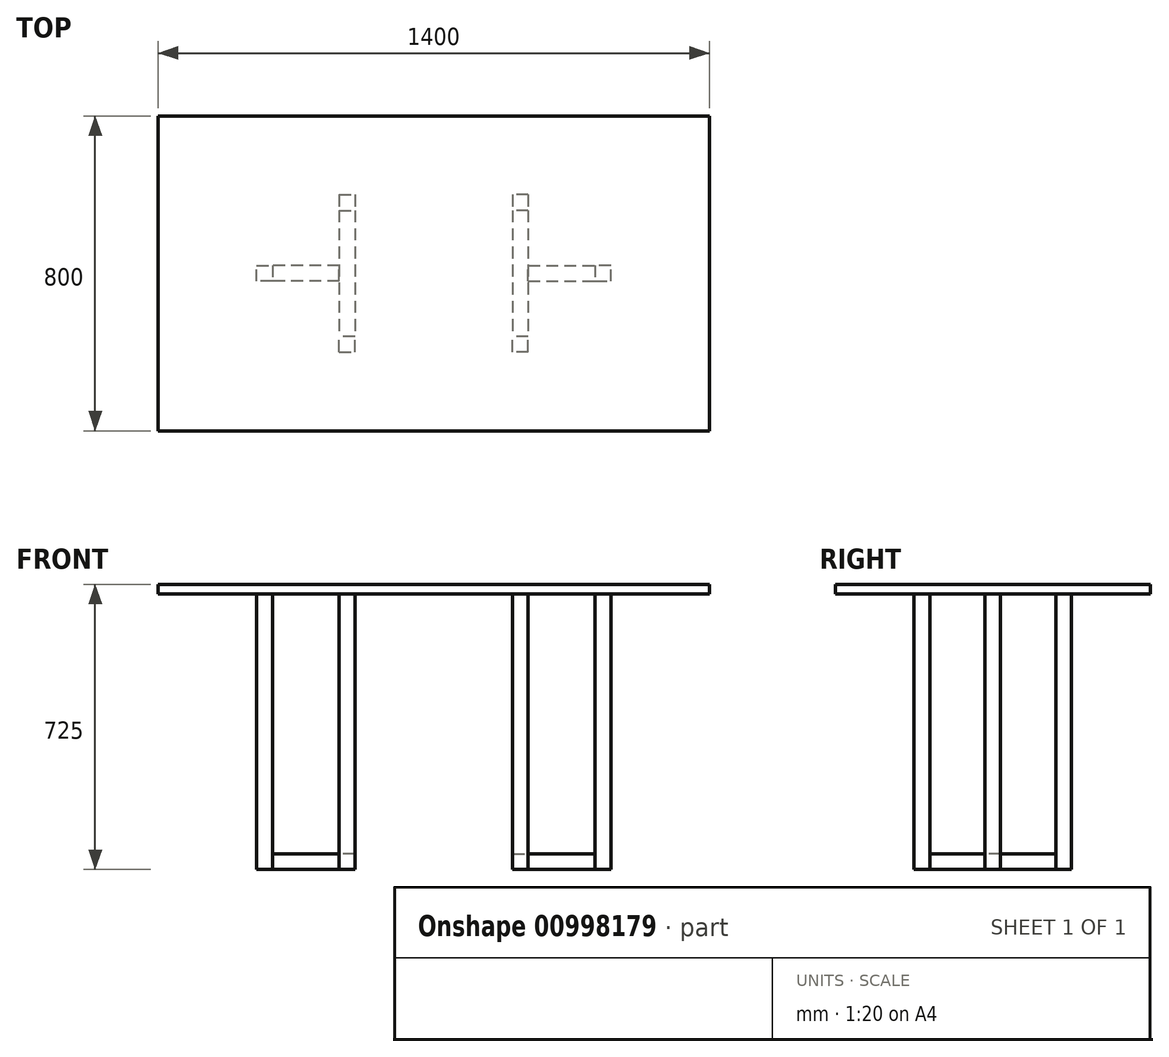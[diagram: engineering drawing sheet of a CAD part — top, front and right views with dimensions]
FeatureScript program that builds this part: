
annotation { "Feature Type Name" : "Feature", "Feature Type Description" : "" }
export const myFeature = defineFeature(function(context is Context, id is Id, definition is map)
    precondition{}
    {
        {
            var Q0;
            Q0=qCreatedBy(makeId("Top.planeOp"),FACE);
            var sketch = newSketch(context, id + "F0", { "sketchPlane" : qUnion([Q0])});
            skLineSegment(sketch, "E0.bottom", {"start": v(0, 0) * mm, "end": v(-1400, 0) * mm, "construction": true});
            skLineSegment(sketch, "E0.top", {"start": v(0, 800) * mm, "end": v(-1400, 800) * mm, "construction": true});
            skLineSegment(sketch, "E0.left", {"start": v(0, 0) * mm, "end": v(0, 800) * mm, "construction": true});
            skLineSegment(sketch, "E0.right", {"start": v(-1400, 0) * mm, "end": v(-1400, 800) * mm, "construction": true});
            skLineSegment(sketch, "E1", {"start": v(-1400, 800) * mm, "end": v(-1400, 600) * mm, "construction": true});
            skLineSegment(sketch, "E2", {"start": v(-700, 800) * mm, "end": v(-700, 0) * mm, "construction": true});
            skLineSegment(sketch, "E3", {"start": v(-1400, 400) * mm, "end": v(0, 400) * mm, "construction": true});
            skLineSegment(sketch, "E4", {"start": v(-1400, 400) * mm, "end": v(-1150, 400) * mm, "construction": true});
            skLineSegment(sketch, "E5", {"start": v(-1400, 600) * mm, "end": v(-940, 600) * mm, "construction": true});
            skLineSegment(sketch, "E6.bottom", {"start": v(-940, 600) * mm, "end": v(-900, 600) * mm});
            skLineSegment(sketch, "E6.top", {"start": v(-940, 560) * mm, "end": v(-900, 560) * mm});
            skLineSegment(sketch, "E6.left", {"start": v(-940, 600) * mm, "end": v(-940, 560) * mm});
            skLineSegment(sketch, "E6.right", {"start": v(-900, 600) * mm, "end": v(-900, 560) * mm});
            skLineSegment(sketch, "E7", {"start": v(-1150, 400) * mm, "end": v(-1150, 420) * mm});
            skLineSegment(sketch, "E8", {"start": v(-1150, 420) * mm, "end": v(-1110, 420) * mm});
            skLineSegment(sketch, "E9", {"start": v(-1110, 420) * mm, "end": v(-1110, 380) * mm});
            skLineSegment(sketch, "E10", {"start": v(-1110, 380) * mm, "end": v(-1150, 380) * mm});
            skLineSegment(sketch, "E11", {"start": v(-1150, 380) * mm, "end": v(-1150, 400) * mm});
            skLineSegment(sketch, "E12.MirrorCS", {"start": v(-940, 240) * mm, "end": v(-900, 240) * mm});
            skLineSegment(sketch, "E13.MirrorCS", {"start": v(-900, 200) * mm, "end": v(-900, 240) * mm});
            skLineSegment(sketch, "E14.MirrorCS", {"start": v(-940, 200) * mm, "end": v(-900, 200) * mm});
            skLineSegment(sketch, "E15.MirrorCS", {"start": v(-940, 200) * mm, "end": v(-940, 240) * mm});
            skLineSegment(sketch, "E16.MirrorCS", {"start": v(-250, 420) * mm, "end": v(-290, 420) * mm});
            skLineSegment(sketch, "E17.MirrorCS", {"start": v(-290, 420) * mm, "end": v(-290, 380) * mm});
            skLineSegment(sketch, "E18.MirrorCS", {"start": v(-290, 380) * mm, "end": v(-250, 380) * mm});
            skLineSegment(sketch, "E19.MirrorCS", {"start": v(-250, 380) * mm, "end": v(-250, 400) * mm});
            skLineSegment(sketch, "E20.MirrorCS", {"start": v(-500, 600) * mm, "end": v(-500, 560) * mm});
            skLineSegment(sketch, "E21.MirrorCS", {"start": v(-460, 600) * mm, "end": v(-500, 600) * mm});
            skLineSegment(sketch, "E22.MirrorCS", {"start": v(-460, 600) * mm, "end": v(-460, 560) * mm});
            skLineSegment(sketch, "E23.MirrorCS", {"start": v(-460, 560) * mm, "end": v(-500, 560) * mm});
            skLineSegment(sketch, "E24.MirrorCS", {"start": v(-500, 200) * mm, "end": v(-500, 240) * mm});
            skLineSegment(sketch, "E25.MirrorCS", {"start": v(-460, 240) * mm, "end": v(-500, 240) * mm});
            skLineSegment(sketch, "E26.MirrorCS", {"start": v(-460, 200) * mm, "end": v(-460, 240) * mm});
            skLineSegment(sketch, "E27.MirrorCS", {"start": v(-460, 200) * mm, "end": v(-500, 200) * mm});
            skLineSegment(sketch, "E28.MirrorCS", {"start": v(-250, 400) * mm, "end": v(-250, 420) * mm});
            skSolve(sketch);
        }
        {
            var Q0;
            Q0 = qSketchRegion(id + "F0", true);
            extrude(context, id + "F1", {"entities" : qUnion([Q0]), "depth" : 700 * mm, "offsetDistance" : 25 * mm});
        }
        {
            var Q0;
            Q0=makeQuery(id+"F1.opExtrude","SWEPT_FACE",FACE,{"disambiguationData":[OSD([sQuery(id+"F0.wireOp",EDGE,"E12.MirrorCS")])]});
            cPlane(context, id + "F2", {"entities" : qUnion([Q0]), "cplaneType" : CPlaneType.OFFSET, "offset" : 0 * mm, "width" : 150 * mm, "height" : 150 * mm});
        }
        {
            var Q0;
            Q0=qCreatedBy(id+"F2.planeOp",FACE);
            var sketch = newSketch(context, id + "F3", { "sketchPlane" : qUnion([Q0])});
            skLineSegment(sketch, "E29", {"start": v(460, 0) * mm, "end": v(500, 0) * mm});
            skLineSegment(sketch, "E30", {"start": v(500, 0) * mm, "end": v(500, 40) * mm});
            skLineSegment(sketch, "E31", {"start": v(500, 40) * mm, "end": v(460, 40) * mm});
            skLineSegment(sketch, "E32", {"start": v(460, 40) * mm, "end": v(460, 0) * mm});
            skLineSegment(sketch, "E33", {"start": v(700, 0) * mm, "end": v(700, 149.7) * mm, "construction": true});
            skLineSegment(sketch, "E34.MirrorCS", {"start": v(900, 40) * mm, "end": v(940, 40) * mm});
            skLineSegment(sketch, "E35.MirrorCS", {"start": v(940, 40) * mm, "end": v(940, 0) * mm});
            skLineSegment(sketch, "E36.MirrorCS", {"start": v(900, 0) * mm, "end": v(900, 40) * mm});
            skLineSegment(sketch, "E37.MirrorCS", {"start": v(940, 0) * mm, "end": v(900, 0) * mm});
            skSolve(sketch);
        }
        {
            var Q0;
            Q0 = qSketchRegion(id + "F3", true);
            extrude(context, id + "F4", {"entities" : qUnion([Q0]), "depth" : 320 * mm, "offsetDistance" : 25 * mm});
        }
        {
            var Q0;
            Q0=makeQuery(id+"F1.opExtrude","SWEPT_FACE",FACE,{"disambiguationData":[OSD([sQuery(id+"F0.wireOp",EDGE,"E17.MirrorCS")])]});
            cPlane(context, id + "F5", {"entities" : qUnion([Q0]), "cplaneType" : CPlaneType.OFFSET, "offset" : 0 * mm, "width" : 150 * mm, "height" : 150 * mm});
        }
        {
            var Q0;
            Q0=qCreatedBy(id+"F5.planeOp",FACE);
            var sketch = newSketch(context, id + "F6", { "sketchPlane" : qUnion([Q0])});
            skLineSegment(sketch, "E38", {"start": v(0, 0) * mm, "end": v(-400, 0) * mm, "construction": true});
            skLineSegment(sketch, "E39", {"start": v(-400, 0) * mm, "end": v(-420, 0) * mm});
            skLineSegment(sketch, "E40", {"start": v(-420, 0) * mm, "end": v(-420, 40) * mm});
            skLineSegment(sketch, "E41", {"start": v(-420, 40) * mm, "end": v(-380, 40) * mm});
            skLineSegment(sketch, "E42", {"start": v(-380, 40) * mm, "end": v(-380, 0) * mm});
            skLineSegment(sketch, "E43", {"start": v(-380, 0) * mm, "end": v(-400, 0) * mm});
            skSolve(sketch);
        }
        {
            var Q0;
            Q0 = qSketchRegion(id + "F6", true);
            extrude(context, id + "F7", {"entities" : qUnion([Q0]), "depth" : 170 * mm, "offsetDistance" : 25 * mm});
        }
        {
            var Q0;
            Q0=makeQuery(id+"F1.opExtrude","SWEPT_FACE",FACE,{"disambiguationData":[OSD([sQuery(id+"F0.wireOp",EDGE,"E9")])]});
            cPlane(context, id + "F8", {"entities" : qUnion([Q0]), "cplaneType" : CPlaneType.OFFSET, "offset" : 0 * mm, "width" : 150 * mm, "height" : 150 * mm});
        }
        {
            var Q0;
            Q0=qCreatedBy(id+"F8.planeOp",FACE);
            var sketch = newSketch(context, id + "F9", { "sketchPlane" : qUnion([Q0])});
            skLineSegment(sketch, "E44", {"start": v(400, 0) * mm, "end": v(420, 0) * mm});
            skLineSegment(sketch, "E45", {"start": v(420, 0) * mm, "end": v(420, 40) * mm});
            skLineSegment(sketch, "E46", {"start": v(420, 40) * mm, "end": v(380, 40) * mm});
            skLineSegment(sketch, "E47", {"start": v(380, 40) * mm, "end": v(380, 0) * mm});
            skLineSegment(sketch, "E48", {"start": v(380, 0) * mm, "end": v(400, 0) * mm});
            skSolve(sketch);
        }
        {
            var Q0;
            Q0 = qSketchRegion(id + "F9", true);
            extrude(context, id + "F10", {"entities" : qUnion([Q0]), "depth" : 170 * mm, "offsetDistance" : 25 * mm});
        }
        {
            var Q0;
            Q0=makeQuery(id+"F1.opExtrude","CAP_FACE",FACE,{"disambiguationData":[OSD([sQuery(id+"F0.wireOp",EDGE,"E20.MirrorCS"),sQuery(id+"F0.wireOp",EDGE,"E21.MirrorCS"),sQuery(id+"F0.wireOp",EDGE,"E22.MirrorCS"),sQuery(id+"F0.wireOp",EDGE,"E23.MirrorCS")])],"isStart":false});
            cPlane(context, id + "F11", {"entities" : qUnion([Q0]), "cplaneType" : CPlaneType.OFFSET, "offset" : 0 * mm, "width" : 150 * mm, "height" : 150 * mm});
        }
        {
            var Q0;
            Q0=qCreatedBy(id+"F11.planeOp",FACE);
            var sketch = newSketch(context, id + "F12", { "sketchPlane" : qUnion([Q0])});
            skLineSegment(sketch, "E49.bottom", {"start": v(0, 0) * mm, "end": v(-1400, 0) * mm});
            skLineSegment(sketch, "E49.top", {"start": v(0, 800) * mm, "end": v(-1400, 800) * mm});
            skLineSegment(sketch, "E49.left", {"start": v(0, 0) * mm, "end": v(0, 800) * mm});
            skLineSegment(sketch, "E49.right", {"start": v(-1400, 0) * mm, "end": v(-1400, 800) * mm});
            skSolve(sketch);
        }
        {
            var Q0;
            Q0 = qSketchRegion(id + "F12", true);
            extrude(context, id + "F13", {"entities" : qUnion([Q0]), "depth" : 25 * mm, "offsetDistance" : 25 * mm});
        }
    });
